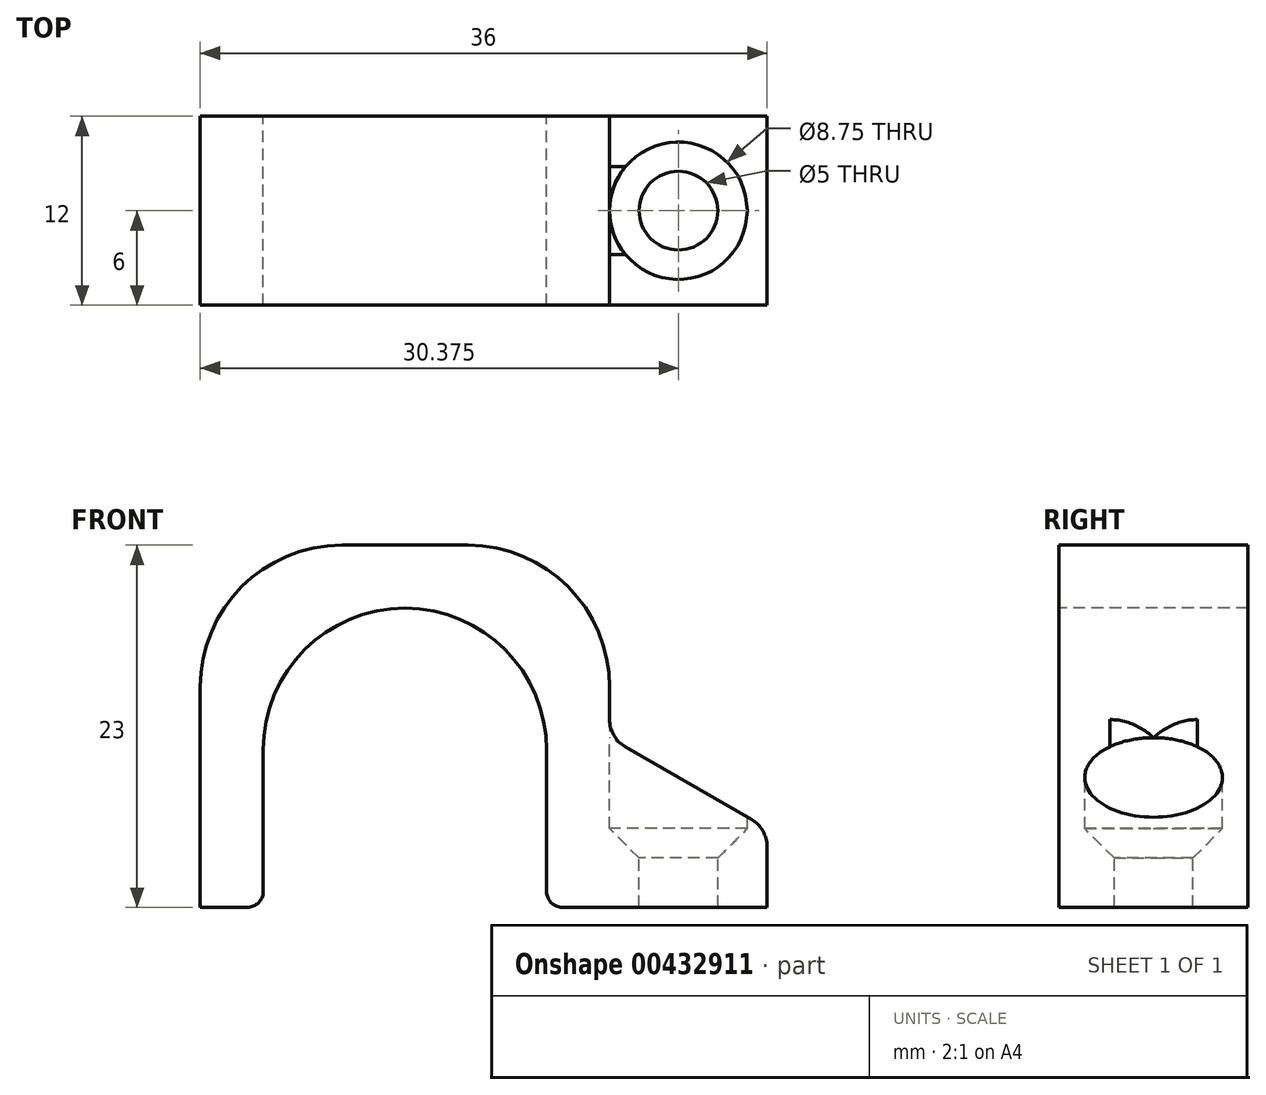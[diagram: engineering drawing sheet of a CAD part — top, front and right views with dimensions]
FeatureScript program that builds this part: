
annotation { "Feature Type Name" : "Feature", "Feature Type Description" : "" }
export const myFeature = defineFeature(function(context is Context, id is Id, definition is map)
    precondition{}
    {
        {
            var Q0;
            Q0=qCreatedBy(makeId("Front.planeOp"),FACE);
            var sketch = newSketch(context, id + "F0", { "sketchPlane" : qUnion([Q0])});
            skLineSegment(sketch, "E0.bottom", {"start": v(-9, 0) * mm, "end": v(9, 0) * mm, "construction": true});
            skLineSegment(sketch, "E0.top", {"start": v(-9, 19) * mm, "end": v(9, 19) * mm});
            skLineSegment(sketch, "E0.left", {"start": v(-9, 0) * mm, "end": v(-9, 19) * mm});
            skLineSegment(sketch, "E0.right", {"start": v(9, 0) * mm, "end": v(9, 19) * mm});
            skPoint(sketch, "E0.middle", {"position": v(0, 9.5) * mm});
            skLineSegment(sketch, "E1", {"start": v(-9, 0) * mm, "end": v(-13, 0) * mm});
            skLineSegment(sketch, "E2", {"start": v(-13, 0) * mm, "end": v(-13, 23) * mm});
            skCircle(sketch, "E3", {"center": v(0, 9.5) * mm, "radius": 8.5 * mm, "construction": true});
            skLineSegment(sketch, "E4", {"start": v(9, 0) * mm, "end": v(23, 0) * mm, "construction": true});
            skLineSegment(sketch, "E5", {"start": v(23, 0) * mm, "end": v(23, 5) * mm});
            skLineSegment(sketch, "E6", {"start": v(23, 5) * mm, "end": v(13, 10.77) * mm});
            skLineSegment(sketch, "E7", {"start": v(13, 10.77) * mm, "end": v(13, 23) * mm});
            skLineSegment(sketch, "E8", {"start": v(13, 23) * mm, "end": v(-13, 23) * mm});
            skLineSegment(sketch, "E9", {"start": v(9, 0) * mm, "end": v(23, 0) * mm});
            skSolve(sketch);
        }
        {
            var Q0;
            Q0 = qSketchRegion(id + "F0", true);
            extrude(context, id + "F1", {"entities" : qUnion([Q0]), "depth" : 6 * mm, "hasSecondDirection" : true, "secondDirectionOppositeDirection" : true, "secondDirectionDepth" : 6 * mm});
        }
        {
            var Q0;
            Q0=makeQuery(id+"F1.opExtrude","SWEPT_EDGE",EDGE,{"disambiguationData":[OSD([sQuery(id+"F0.wireOp",EDGE,"E0.top"),sQuery(id+"F0.wireOp",EDGE,"E0.left")])]});
            var Q1;
            Q1=makeQuery(id+"F1.opExtrude","SWEPT_EDGE",EDGE,{"disambiguationData":[OSD([sQuery(id+"F0.wireOp",EDGE,"E0.top"),sQuery(id+"F0.wireOp",EDGE,"E0.right")])]});
            var Q2;
            Q2=makeQuery(id+"F1.opExtrude","SWEPT_EDGE",EDGE,{"disambiguationData":[OSD([sQuery(id+"F0.wireOp",EDGE,"E2"),sQuery(id+"F0.wireOp",EDGE,"E8")])]});
            var Q3;
            Q3=makeQuery(id+"F1.opExtrude","SWEPT_EDGE",EDGE,{"disambiguationData":[OSD([sQuery(id+"F0.wireOp",EDGE,"E7"),sQuery(id+"F0.wireOp",EDGE,"E8")])]});
            fillet(context, id + "F2", {"entities" : qUnion([Q0, Q1, Q2, Q3]), "radius" : 9 * mm, "tangentPropagation" : true, "allowEdgeOverflow" : false});
        }
        {
            var Q0;
            Q0=makeQuery(id+"F1.opExtrude","SWEPT_FACE",FACE,{"disambiguationData":[OSD([sQuery(id+"F0.wireOp",EDGE,"E8")])]});
            var sketch = newSketch(context, id + "F3", { "sketchPlane" : qUnion([Q0])});
            skLineSegment(sketch, "E10", {"start": v(0, 0) * mm, "end": v(13, 0) * mm});
            skCircle(sketch, "E11", {"center": v(17.38, 0) * mm, "radius": 4.38 * mm});
            skSolve(sketch);
        }
        {
            var Q0;
            Q0 = qSketchRegion(id + "F3", true);
            extrude(context, id + "F4", {"entities" : qUnion([Q0]), "operationType" : NewBodyOperationType.REMOVE, "oppositeDirection" : true, "depth" : 18 * mm});
        }
        {
            var Q0;
            Q0=makeQuery(id+"F4.boolean.opBoolean","COPY",FACE,{"derivedFrom":makeQuery(id+"F4.opExtrude","CAP_FACE",FACE,{"disambiguationData":[OSD([sQuery(id+"F3.wireOp",EDGE,"E11")])],"isStart":false})});
            var sketch = newSketch(context, id + "F5", { "sketchPlane" : qUnion([Q0])});
            skCircle(sketch, "E12", {"center": v(17.37, 0) * mm, "radius": 2.5 * mm});
            skSolve(sketch);
        }
        {
            var Q0;
            Q0=sQuery(id+"F5.wireOp",VERTEX,"E12.center");
            var Q1;
            Q1=makeQuery(id+"F1.opExtrude","SWEPT_BODY",BODY,{"disambiguationData":[OSD([sQuery(id+"F0.wireOp",EDGE,"E0.top"),sQuery(id+"F0.wireOp",EDGE,"E0.left"),sQuery(id+"F0.wireOp",EDGE,"E0.right"),sQuery(id+"F0.wireOp",EDGE,"E1"),sQuery(id+"F0.wireOp",EDGE,"E2"),sQuery(id+"F0.wireOp",EDGE,"E5"),sQuery(id+"F0.wireOp",EDGE,"E6"),sQuery(id+"F0.wireOp",EDGE,"E7"),sQuery(id+"F0.wireOp",EDGE,"E8"),sQuery(id+"F0.wireOp",EDGE,"E9")])]});
            hole(context, id + "F6", {"style" : HoleStyle.C_SINK, "endStyle" : HoleEndStyle.THROUGH, "holeDiameter" : 5 * mm, "cSinkDiameter" : 8.75 * mm, "cSinkAngle" : 90 * degree, "isTappedThrough" : true, "tappedDepth" : 12 * mm, "tapClearance" : 3, "startFromSketch" : true, "locations" : qUnion([Q0]), "scope" : qUnion([Q1])});
        }
        {
            var Q0;
            {var subQ0=sQuery(id+"F0.wireOp",EDGE,"E7");var subQ1=sQuery(id+"F0.wireOp",EDGE,"E6");Q0=makeQuery(id+"F4.boolean.opBoolean","SPLIT",EDGE,{"disambiguationData":[TD([makeQuery(id+"F1.opExtrude","CAP_FACE",FACE,{"disambiguationData":[OSD([sQuery(id+"F0.wireOp",EDGE,"E0.top"),sQuery(id+"F0.wireOp",EDGE,"E0.left"),sQuery(id+"F0.wireOp",EDGE,"E0.right"),sQuery(id+"F0.wireOp",EDGE,"E1"),sQuery(id+"F0.wireOp",EDGE,"E2"),sQuery(id+"F0.wireOp",EDGE,"E5"),subQ1,subQ0,sQuery(id+"F0.wireOp",EDGE,"E8"),sQuery(id+"F0.wireOp",EDGE,"E9")])],"isStart":true})])],"derivedFrom":makeQuery(id+"F1.opExtrude","SWEPT_EDGE",EDGE,{"disambiguationData":[OSD([subQ1,subQ0])]})});}
            var Q1;
            Q1=makeQuery(id+"F1.opExtrude","SWEPT_EDGE",EDGE,{"disambiguationData":[OSD([sQuery(id+"F0.wireOp",EDGE,"E5"),sQuery(id+"F0.wireOp",EDGE,"E6")])]});
            fillet(context, id + "F7", {"entities" : qUnion([Q0, Q1]), "radius" : 2 * mm, "tangentPropagation" : true, "allowEdgeOverflow" : false});
        }
        {
            var Q0;
            Q0=makeQuery(id+"F1.opExtrude","SWEPT_EDGE",EDGE,{"disambiguationData":[OSD([sQuery(id+"F0.wireOp",EDGE,"E0.left"),sQuery(id+"F0.wireOp",EDGE,"E1")])]});
            var Q1;
            Q1=makeQuery(id+"F1.opExtrude","SWEPT_EDGE",EDGE,{"disambiguationData":[OSD([sQuery(id+"F0.wireOp",EDGE,"E0.right"),sQuery(id+"F0.wireOp",EDGE,"E9")])]});
            fillet(context, id + "F8", {"entities" : qUnion([Q0, Q1]), "radius" : 1 * mm, "tangentPropagation" : true, "allowEdgeOverflow" : false});
        }
    });
